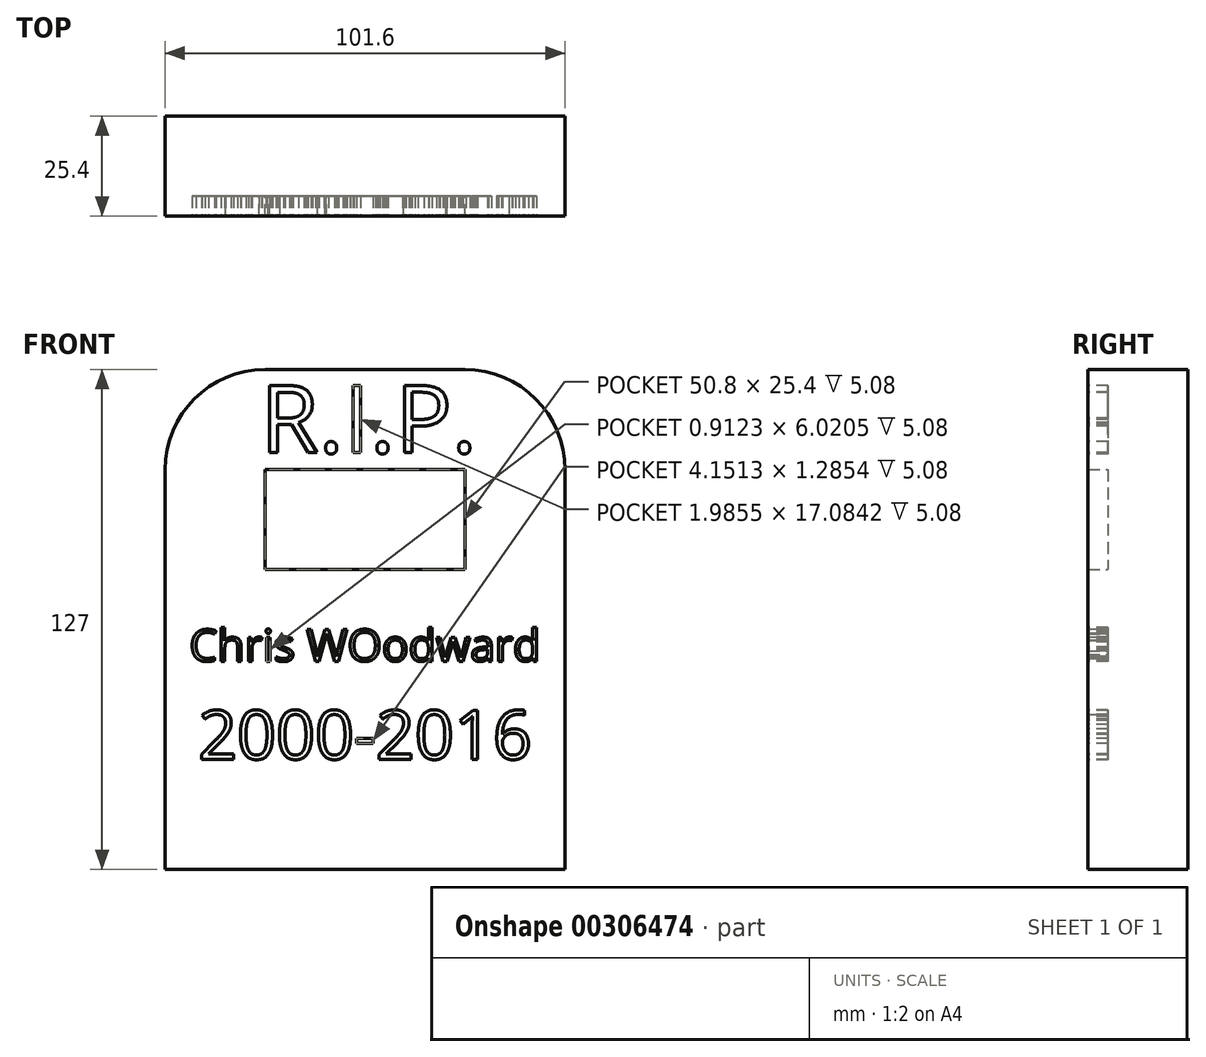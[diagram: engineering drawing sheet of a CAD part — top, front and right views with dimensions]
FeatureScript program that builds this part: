
annotation { "Feature Type Name" : "Feature", "Feature Type Description" : "" }
export const myFeature = defineFeature(function(context is Context, id is Id, definition is map)
    precondition{}
    {
        {
            var Q0;
            Q0=qCreatedBy(makeId("Front.planeOp"),FACE);
            var sketch = newSketch(context, id + "F0", { "sketchPlane" : qUnion([Q0])});
            skLineSegment(sketch, "E0.bottom", {"start": v(-46.19, -61.39) * mm, "end": v(55.41, -61.39) * mm});
            skLineSegment(sketch, "E0.top", {"start": v(-20.79, 65.61) * mm, "end": v(30.01, 65.61) * mm});
            skLineSegment(sketch, "E0.left", {"start": v(-46.19, -61.39) * mm, "end": v(-46.19, 40.21) * mm});
            skLineSegment(sketch, "E0.right", {"start": v(55.41, -61.39) * mm, "end": v(55.41, 40.21) * mm});
            skPoint(sketch, "E1.visualSharp", {"position": v(-46.19, 65.61) * mm});
            skArc(sketch, "E1.filletArc", {"start": v(-20.79, 65.61) * mm, "mid": v(-38.75, 58.17) * mm, "end": v(-46.19, 40.21) * mm});
            skPoint(sketch, "E2.visualSharp", {"position": v(55.41, 65.61) * mm});
            skArc(sketch, "E2.filletArc", {"start": v(55.41, 40.21) * mm, "mid": v(47.98, 58.17) * mm, "end": v(30.01, 65.61) * mm});
            skLineSegment(sketch, "E3.bottom", {"start": v(-20.79, 40.21) * mm, "end": v(30.01, 40.21) * mm});
            skLineSegment(sketch, "E3.top", {"start": v(-20.79, 14.81) * mm, "end": v(30.01, 14.81) * mm});
            skLineSegment(sketch, "E3.left", {"start": v(-20.79, 40.21) * mm, "end": v(-20.79, 14.81) * mm});
            skLineSegment(sketch, "E3.right", {"start": v(30.01, 40.21) * mm, "end": v(30.01, 14.81) * mm});
            skSolve(sketch);
        }
        {
            var Q0;
            Q0 = qSketchRegion(id + "F0", true);
            extrude(context, id + "F1", {"entities" : qUnion([Q0]), "depth" : 25.4 * mm});
        }
        {
            var Q0;
            Q0=makeQuery(id+"F0.imprint","IMPRINT",FACE,{"disambiguationData":[TD([[makeQuery(id+"F0.imprint","IMPRINT",EDGE,{"derivedFrom":sQuery(id+"F0.wireOp",EDGE,"E3.bottom")}),-1.0]])]});
            extrude(context, id + "F2", {"entities" : qUnion([Q0]), "operationType" : NewBodyOperationType.ADD, "depth" : 20.32 * mm});
        }
        {
            var Q0;
            Q0=makeQuery(id+"F1.opExtrude","CAP_FACE",FACE,{"disambiguationData":[OSD([sQuery(id+"F0.wireOp",EDGE,"E0.bottom"),sQuery(id+"F0.wireOp",EDGE,"E0.top"),sQuery(id+"F0.wireOp",EDGE,"E0.left"),sQuery(id+"F0.wireOp",EDGE,"E0.right"),sQuery(id+"F0.wireOp",EDGE,"E1.filletArc"),sQuery(id+"F0.wireOp",EDGE,"E2.filletArc"),sQuery(id+"F0.wireOp",EDGE,"E3.bottom"),sQuery(id+"F0.wireOp",EDGE,"E3.top"),sQuery(id+"F0.wireOp",EDGE,"E3.left"),sQuery(id+"F0.wireOp",EDGE,"E3.right")])],"isStart":false});
            var sketch = newSketch(context, id + "F3", { "sketchPlane" : qUnion([Q0])});
            skText(sketch, "E4", { "text": "R.I.P.", "fontName": "OpenSans-Regular.ttf"});
            const initialGuessF3  = {"E4": [-0.02195, 0.04449, 1, 0, 0.01723]};
            skSetInitialGuess(sketch, initialGuessF3);
            skSolve(sketch);
        }
        {
            var Q0;
            Q0=makeQuery(id+"F3.imprint","IMPRINT",FACE,{"disambiguationData":[TD([[makeQuery(id+"F3.imprint","IMPRINT",EDGE,{"derivedFrom":sQuery(id+"F3.wireOp",EDGE,"E4.sketch_text.stroke-0")}),1.0]])]});
            var sketch = newSketch(context, id + "F4", { "sketchPlane" : qUnion([Q0])});
            skText(sketch, "E5", { "text": "Chris WOodward", "fontName": "OpenSans-Regular.ttf"});
            skText(sketch, "E6", { "text": "2000-2016", "fontName": "OpenSans-Regular.ttf"});
            const initialGuessF4  = {"E5": [-0.03999, -0.00849, 1, 0, 0.0081], "E6": [-0.0378, -0.03338, 1, 0, 0.01247]};
            skSetInitialGuess(sketch, initialGuessF4);
            skSolve(sketch);
        }
        {
            var Q0;
            Q0 = qSketchRegion(id + "F4", true);
            extrude(context, id + "F5", {"entities" : qUnion([Q0]), "operationType" : NewBodyOperationType.REMOVE, "oppositeDirection" : true, "depth" : 5.08 * mm});
        }
        {
            var Q0;
            Q0 = qSketchRegion(id + "F3", true);
            extrude(context, id + "F6", {"entities" : qUnion([Q0]), "operationType" : NewBodyOperationType.REMOVE, "oppositeDirection" : true, "depth" : 5.08 * mm});
        }
    });
